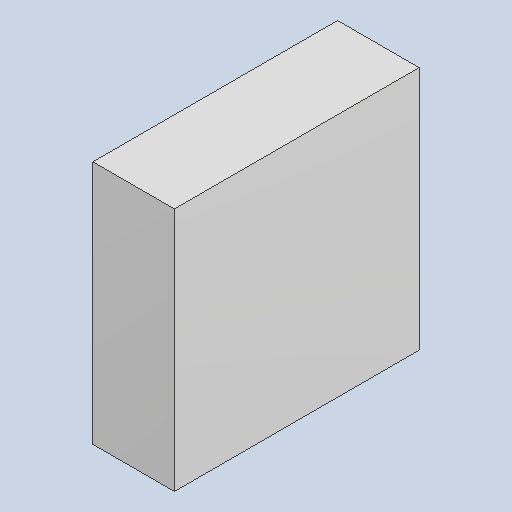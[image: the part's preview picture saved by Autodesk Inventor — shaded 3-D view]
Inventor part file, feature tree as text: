
AUTODESK INVENTOR PART (.ipt)
format: ipt  version: 2023.4 (Build 274418000, 418)  size: 81,408 bytes
history: native  units: mm
features: extrude x1
ambient origin geometry x8: Origin, YZ Plane, XZ Plane, XY Plane, X Axis, Y Axis, Z Axis, Center Point
bodies: Solid1 (feature_tree)
feature tree (1):
  extrude  "Extruded_4"  [1 undecoded]
note: 1 required parameter value undecoded (feature->parameter linkage not recoverable at this tier; creation-order binding heuristic only, values carry confidence <= 0.55)
